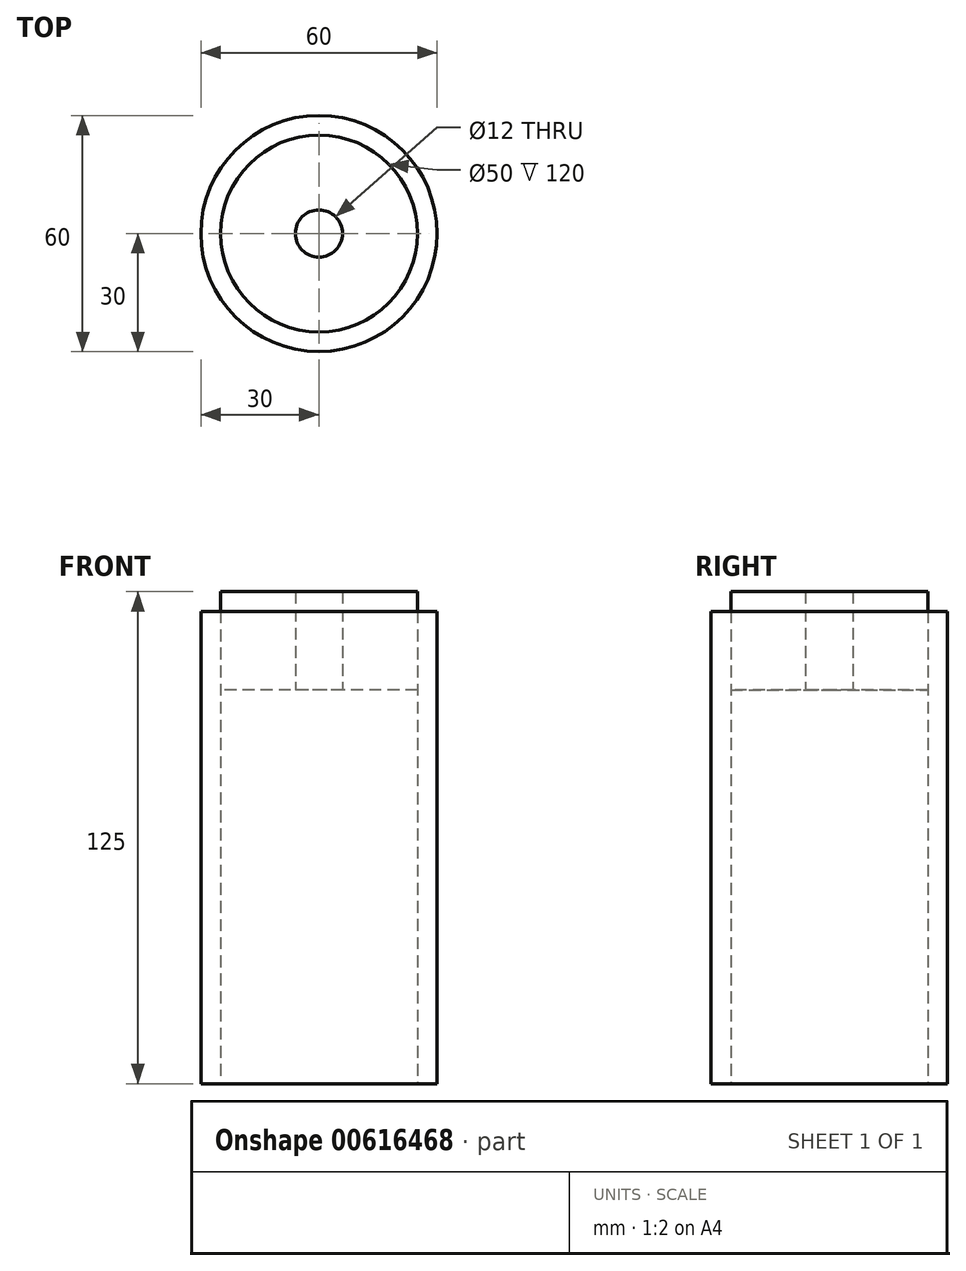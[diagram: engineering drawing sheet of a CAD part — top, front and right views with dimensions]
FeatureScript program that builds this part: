
annotation { "Feature Type Name" : "Feature", "Feature Type Description" : "" }
export const myFeature = defineFeature(function(context is Context, id is Id, definition is map)
    precondition{}
    {
        {
            var Q0;
            Q0=qCreatedBy(makeId("Front.planeOp"),FACE);
            var sketch = newSketch(context, id + "F0", { "sketchPlane" : qUnion([Q0])});
            skLineSegment(sketch, "E0.bottom", {"start": v(0, 0) * mm, "end": v(-30, 0) * mm});
            skLineSegment(sketch, "E0.left", {"start": v(0, 0) * mm, "end": v(0, 120) * mm});
            skLineSegment(sketch, "E0.right", {"start": v(-30, 0) * mm, "end": v(-30, 120) * mm});
            skPoint(sketch, "E1.visualSharp", {"position": v(-30, 119.87) * mm});
            skLineSegment(sketch, "E2", {"start": v(0, 120) * mm, "end": v(-30, 120) * mm});
            skSolve(sketch);
        }
        {
            var Q0;
            Q0=qSketchRegion(id+"F0",true);
            var Q1;
            Q1=sQuery(id+"F0.wireOp",EDGE,"E0.left");
            revolve(context, id + "F1", {"entities" : qUnion([Q0]), "axis" : qUnion([Q1]), "revolveType" : RevolveType.FULL});
        }
        {
            var Q0;
            Q0=qCreatedBy(makeId("Top.planeOp"),FACE);
            var sketch = newSketch(context, id + "F2", { "sketchPlane" : qUnion([Q0])});
            skCircle(sketch, "E3", {"center": v(0, 0) * mm, "radius": 25 * mm});
            skSolve(sketch);
        }
        {
            var Q0;
            Q0=qSketchRegion(id+"F2",true);
            extrude(context, id + "F3", {"entities" : qUnion([Q0]), "operationType" : NewBodyOperationType.REMOVE, "endBound" : BoundingType.THROUGH_ALL, "depth" : 100 * mm, "offsetDistance" : 25 * mm});
        }
        {
            var Q0;
            Q0=qCreatedBy(makeId("Top.planeOp"),FACE);
            var sketch = newSketch(context, id + "F4", { "sketchPlane" : qUnion([Q0])});
            skCircle(sketch, "E4", {"center": v(0, 0) * mm, "radius": 5 * mm});
            skSolve(sketch);
        }
        {
            var Q0;
            Q0=qSketchRegion(id+"F4",true);
            extrude(context, id + "F5", {"entities" : qUnion([Q0]), "operationType" : NewBodyOperationType.REMOVE, "endBound" : BoundingType.THROUGH_ALL, "depth" : 25 * mm, "offsetDistance" : 25 * mm});
        }
        {
            var Q0;
            Q0=qCreatedBy(makeId("Top.planeOp"),FACE);
            cPlane(context, id + "F6", {"entities" : qUnion([Q0]), "cplaneType" : CPlaneType.OFFSET, "offset" : 100 * mm, "width" : 150 * mm, "height" : 150 * mm});
        }
        {
            var Q0;
            Q0=qCreatedBy(id+"F6.planeOp",FACE);
            var sketch = newSketch(context, id + "F7", { "sketchPlane" : qUnion([Q0])});
            skCircle(sketch, "E5.0", {"center": v(0, 0) * mm, "radius": 25 * mm});
            skCircle(sketch, "E6", {"center": v(0, 0) * mm, "radius": 6 * mm});
            skSolve(sketch);
        }
        {
            var Q0;
            Q0 = qSketchRegion(id + "F7", true);
            extrude(context, id + "F8", {"entities" : qUnion([Q0]), "depth" : 25 * mm, "offsetDistance" : 25 * mm});
        }
    });
